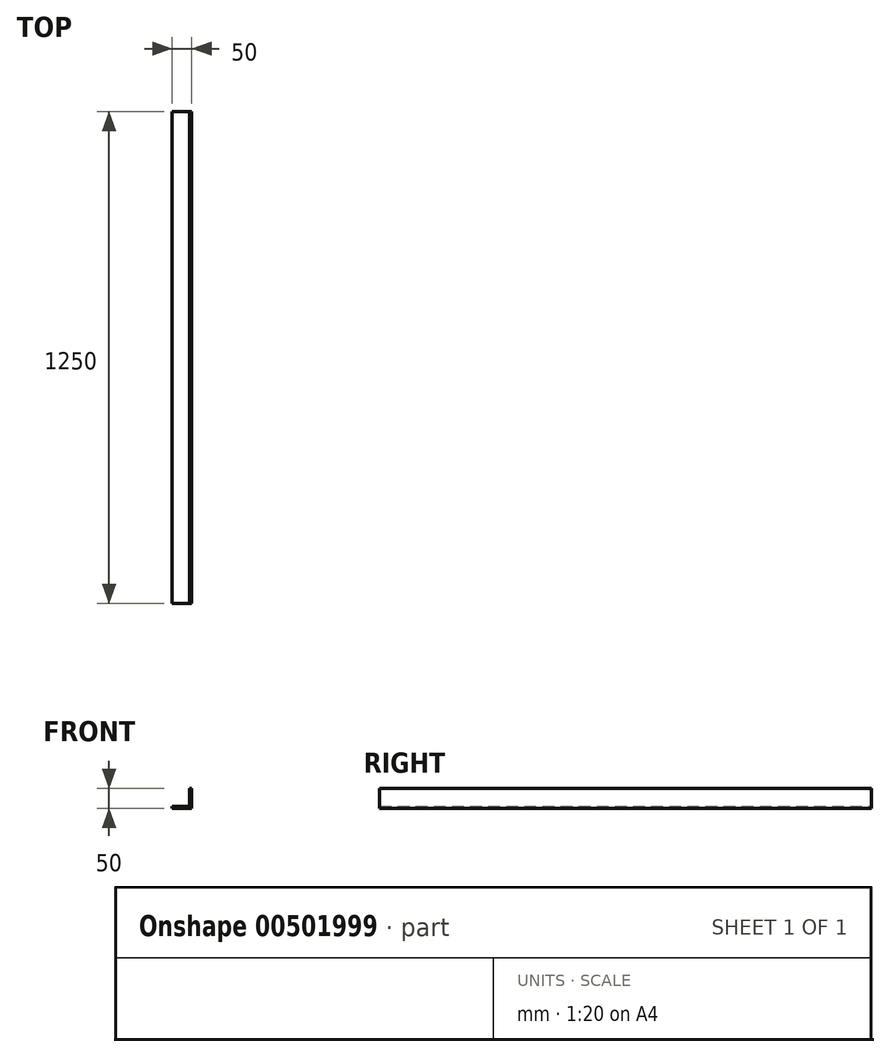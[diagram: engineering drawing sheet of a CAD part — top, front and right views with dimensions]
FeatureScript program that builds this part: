
annotation { "Feature Type Name" : "Feature", "Feature Type Description" : "" }
export const myFeature = defineFeature(function(context is Context, id is Id, definition is map)
    precondition{}
    {
        {
            var Q0;
            Q0=qCreatedBy(makeId("Front.planeOp"),FACE);
            var sketch = newSketch(context, id + "F0", { "sketchPlane" : qUnion([Q0])});
            skLineSegment(sketch, "E0", {"start": v(0, 0) * mm, "end": v(0, 50) * mm});
            skLineSegment(sketch, "E1", {"start": v(0, 50) * mm, "end": v(-5, 50) * mm});
            skLineSegment(sketch, "E2", {"start": v(-5, 50) * mm, "end": v(-5, 5) * mm});
            skLineSegment(sketch, "E3", {"start": v(-5, 5) * mm, "end": v(-50, 5) * mm});
            skLineSegment(sketch, "E4", {"start": v(-50, 5) * mm, "end": v(-50, 0) * mm});
            skLineSegment(sketch, "E5", {"start": v(-50, 0) * mm, "end": v(0, 0) * mm});
            skSolve(sketch);
        }
        {
            var Q0;
            Q0 = qSketchRegion(id + "F0", true);
            extrude(context, id + "F1", {"entities" : qUnion([Q0]), "depth" : 1250 * mm, "offsetDistance" : 25 * mm});
        }
    });
